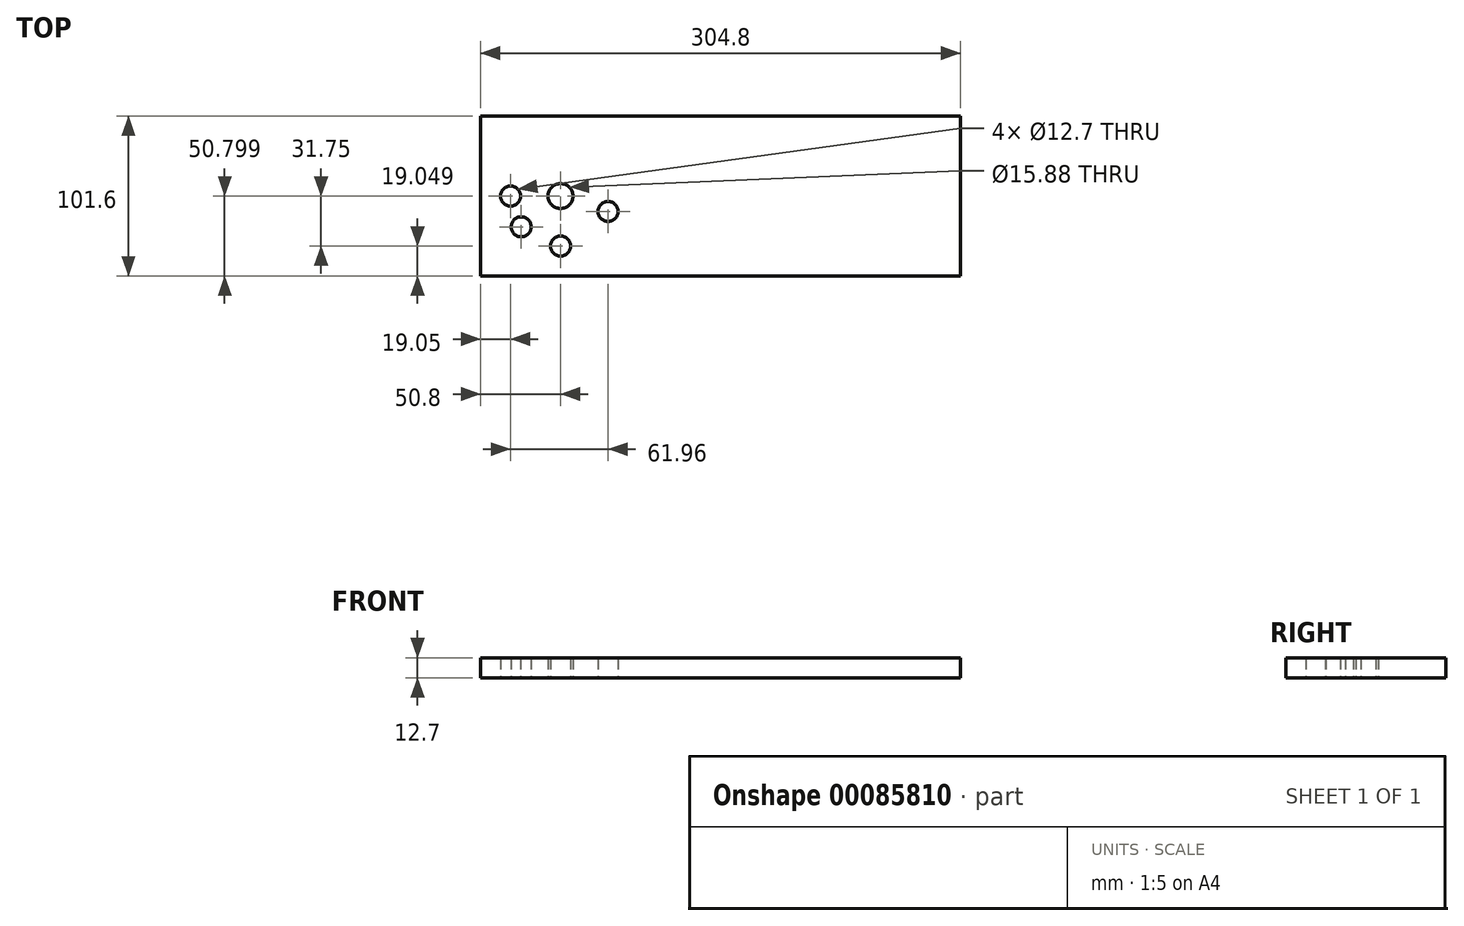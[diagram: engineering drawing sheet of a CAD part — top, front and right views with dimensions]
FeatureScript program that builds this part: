
annotation { "Feature Type Name" : "Feature", "Feature Type Description" : "" }
export const myFeature = defineFeature(function(context is Context, id is Id, definition is map)
    precondition{}
    {
        {
            var Q0;
            Q0=qCreatedBy(makeId("Top.planeOp"),FACE);
            var sketch = newSketch(context, id + "F0", { "sketchPlane" : qUnion([Q0])});
            skPoint(sketch, "E0", {"position": v(-53.4, 28.23) * mm});
            skPoint(sketch, "E1", {"position": v(-53.4, 25.06) * mm});
            skPoint(sketch, "E2", {"position": v(-53.4, 53.63) * mm});
            skPoint(sketch, "E3", {"position": v(-53.4, 12.36) * mm});
            skPoint(sketch, "E4", {"position": v(-53.4, -19.4) * mm});
            skPoint(sketch, "E5", {"position": v(-92.66, 25.06) * mm});
            skPoint(sketch, "E6", {"position": v(-23.18, 2.59) * mm});
            skPoint(sketch, "E7", {"position": v(-85.14, 12.36) * mm});
            skPoint(sketch, "E8", {"position": v(-78.42, -7.18) * mm});
            skPoint(sketch, "E9", {"position": v(-20.86, 37.76) * mm});
            skPoint(sketch, "E10", {"position": v(-12.12, 12.36) * mm});
            skLineSegment(sketch, "E11", {"start": v(-2.6, 63.16) * mm, "end": v(-104.2, 63.16) * mm});
            skLineSegment(sketch, "E12", {"start": v(-104.2, 63.16) * mm, "end": v(-104.2, -38.44) * mm});
            skLineSegment(sketch, "E13", {"start": v(-104.2, -38.44) * mm, "end": v(-2.6, -38.44) * mm});
            skCircle(sketch, "E14", {"center": v(-53.4, 53.63) * mm, "radius": 1.27 * mm});
            skCircle(sketch, "E15", {"center": v(-92.66, 25.06) * mm, "radius": 1.27 * mm});
            skCircle(sketch, "E16", {"center": v(-85.14, 12.36) * mm, "radius": 1.27 * mm});
            skCircle(sketch, "E17", {"center": v(-78.42, -7.18) * mm, "radius": 1.27 * mm});
            skCircle(sketch, "E18", {"center": v(-53.4, -19.4) * mm, "radius": 1.27 * mm});
            skCircle(sketch, "E19", {"center": v(-23.18, 2.59) * mm, "radius": 1.27 * mm});
            skCircle(sketch, "E20", {"center": v(-12.12, 12.36) * mm, "radius": 1.27 * mm});
            skCircle(sketch, "E21", {"center": v(-20.86, 37.76) * mm, "radius": 1.27 * mm});
            skCircle(sketch, "E22", {"center": v(-53.4, 12.36) * mm, "radius": 1.27 * mm});
            skLineSegment(sketch, "E23", {"start": v(200.6, 63.16) * mm, "end": v(200.6, -38.44) * mm});
            skLineSegment(sketch, "E24", {"start": v(-2.6, -38.44) * mm, "end": v(200.6, -38.44) * mm});
            skLineSegment(sketch, "E25", {"start": v(-2.6, 63.16) * mm, "end": v(200.6, 63.16) * mm});
            skSolve(sketch);
        }
        {
            var Q0;
            Q0=makeQuery(id+"F0.imprint","IMPRINT",FACE,{"disambiguationData":[TD([[makeQuery(id+"F0.imprint","IMPRINT",EDGE,{"derivedFrom":sQuery(id+"F0.wireOp",EDGE,"E15")}),1.0]])]});
            var Q1;
            Q1=makeQuery(id+"F0.imprint","IMPRINT",FACE,{"disambiguationData":[TD([[makeQuery(id+"F0.imprint","IMPRINT",EDGE,{"derivedFrom":sQuery(id+"F0.wireOp",EDGE,"E14")}),1.0]])]});
            var Q2;
            Q2=makeQuery(id+"F0.imprint","IMPRINT",FACE,{"disambiguationData":[TD([[makeQuery(id+"F0.imprint","IMPRINT",EDGE,{"derivedFrom":sQuery(id+"F0.wireOp",EDGE,"E21")}),1.0]])]});
            var Q3;
            {var subQ0=sQuery(id+"F0.wireOp",EDGE,"E20");var subQ1=sQuery(id+"F0.wireOp",EDGE,"kDzNyt80-dS94-SnEu-0VYT-oXaxEeU8iF4R");var subQ2=makeQuery(id+"F0.imprint","INTERSECT",VERTEX,{"disambiguationData":[OD(0.0)],"derivedFrom":[subQ1,subQ0]});Q3=makeQuery(id+"F0.imprint","IMPRINT",FACE,{"disambiguationData":[TD([[makeQuery(id+"F0.imprint","IMPRINT",EDGE,{"disambiguationData":[TD([[subQ2,1.0]])],"derivedFrom":subQ1}),-1.0]])]});}
            var Q4;
            {var subQ0=sQuery(id+"F0.wireOp",EDGE,"E20");var subQ1=sQuery(id+"F0.wireOp",EDGE,"kDzNyt80-dS94-SnEu-0VYT-oXaxEeU8iF4R");var subQ2=makeQuery(id+"F0.imprint","INTERSECT",VERTEX,{"disambiguationData":[OD(0.0)],"derivedFrom":[subQ1,subQ0]});Q4=makeQuery(id+"F0.imprint","IMPRINT",FACE,{"disambiguationData":[TD([[makeQuery(id+"F0.imprint","IMPRINT",EDGE,{"disambiguationData":[TD([[subQ2,1.0]])],"derivedFrom":subQ1}),1.0]])]});}
            var Q5;
            Q5=makeQuery(id+"F0.imprint","IMPRINT",FACE,{"disambiguationData":[TD([[makeQuery(id+"F0.imprint","IMPRINT",EDGE,{"derivedFrom":sQuery(id+"F0.wireOp",EDGE,"E11")}),1.0]])]});
            var Q6;
            Q6=makeQuery(id+"F0.imprint","IMPRINT",FACE,{"disambiguationData":[TD([[makeQuery(id+"F0.imprint","IMPRINT",EDGE,{"derivedFrom":sQuery(id+"F0.wireOp",EDGE,"E20")}),1.0]])]});
            extrude(context, id + "F1", {"entities" : qUnion([Q0, Q1, Q2, Q3, Q4, Q5, Q6]), "depth" : 12.7 * mm, "offsetDistance" : 25.4 * mm});
        }
        {
            var Q0;
            Q0=makeQuery(id+"F1.opExtrude","CAP_FACE",FACE,{"disambiguationData":[OSD([sQuery(id+"F0.wireOp",EDGE,"E11"),sQuery(id+"F0.wireOp",EDGE,"E12"),sQuery(id+"F0.wireOp",EDGE,"E13"),sQuery(id+"F0.wireOp",EDGE,"sKdmvjwX-j8QO-bxV5-SpKZ-w8j0p7tcOjNn"),sQuery(id+"F0.wireOp",EDGE,"E14"),sQuery(id+"F0.wireOp",EDGE,"E15"),sQuery(id+"F0.wireOp",EDGE,"E16"),sQuery(id+"F0.wireOp",EDGE,"E17"),sQuery(id+"F0.wireOp",EDGE,"E18"),sQuery(id+"F0.wireOp",EDGE,"E19"),sQuery(id+"F0.wireOp",EDGE,"E20"),sQuery(id+"F0.wireOp",EDGE,"E21"),sQuery(id+"F0.wireOp",EDGE,"E22")])],"isStart":false});
            var sketch = newSketch(context, id + "F2", { "sketchPlane" : qUnion([Q0])});
            skPoint(sketch, "E26", {"position": v(-53.4, 53.63) * mm});
            skPoint(sketch, "E27", {"position": v(-20.86, 37.76) * mm});
            skPoint(sketch, "E28", {"position": v(-12.12, 12.36) * mm});
            skPoint(sketch, "E29", {"position": v(-23.18, 2.59) * mm});
            skPoint(sketch, "E30", {"position": v(-53.4, -19.4) * mm});
            skPoint(sketch, "E31", {"position": v(-78.42, -7.18) * mm});
            skPoint(sketch, "E32", {"position": v(-85.14, 12.36) * mm});
            skPoint(sketch, "E33", {"position": v(-92.66, 25.06) * mm});
            skPoint(sketch, "E34", {"position": v(-53.4, 12.36) * mm});
            skSolve(sketch);
        }
        {
            var Q0;
            Q0=sQuery(id+"F2.wireOp",VERTEX,"E34");
            var Q1;
            Q1=makeQuery(id+"F1.opExtrude","SWEPT_BODY",BODY,{"disambiguationData":[OSD([sQuery(id+"F0.wireOp",EDGE,"E11"),sQuery(id+"F0.wireOp",EDGE,"E12"),sQuery(id+"F0.wireOp",EDGE,"E13"),sQuery(id+"F0.wireOp",EDGE,"sKdmvjwX-j8QO-bxV5-SpKZ-w8j0p7tcOjNn"),sQuery(id+"F0.wireOp",EDGE,"E14"),sQuery(id+"F0.wireOp",EDGE,"E15"),sQuery(id+"F0.wireOp",EDGE,"E16"),sQuery(id+"F0.wireOp",EDGE,"E17"),sQuery(id+"F0.wireOp",EDGE,"E18"),sQuery(id+"F0.wireOp",EDGE,"E19"),sQuery(id+"F0.wireOp",EDGE,"E20"),sQuery(id+"F0.wireOp",EDGE,"E21"),sQuery(id+"F0.wireOp",EDGE,"E22")])]});
            hole(context, id + "F3", {"style" : HoleStyle.SIMPLE, "endStyle" : HoleEndStyle.THROUGH, "holeDiameter" : 15.88 * mm, "majorDiameter" : 6.35 * mm, "tappedDepth" : 12.7 * mm, "tapClearance" : 3, "startFromSketch" : true, "locations" : qUnion([Q0]), "scope" : qUnion([Q1])});
        }
        {
            var Q0;
            Q0=makeQuery(id+"F1.opExtrude","CAP_FACE",FACE,{"disambiguationData":[OSD([sQuery(id+"F0.wireOp",EDGE,"E11"),sQuery(id+"F0.wireOp",EDGE,"E12"),sQuery(id+"F0.wireOp",EDGE,"E13"),sQuery(id+"F0.wireOp",EDGE,"sKdmvjwX-j8QO-bxV5-SpKZ-w8j0p7tcOjNn"),sQuery(id+"F0.wireOp",EDGE,"E14"),sQuery(id+"F0.wireOp",EDGE,"E15"),sQuery(id+"F0.wireOp",EDGE,"E16"),sQuery(id+"F0.wireOp",EDGE,"E17"),sQuery(id+"F0.wireOp",EDGE,"E18"),sQuery(id+"F0.wireOp",EDGE,"E19"),sQuery(id+"F0.wireOp",EDGE,"E20"),sQuery(id+"F0.wireOp",EDGE,"E21"),sQuery(id+"F0.wireOp",EDGE,"E22")])],"isStart":true});
            var sketch = newSketch(context, id + "F4", { "sketchPlane" : qUnion([Q0])});
            skPoint(sketch, "E35", {"position": v(-53.4, -53.63) * mm});
            skSolve(sketch);
        }
        {
            var Q0;
            Q0=makeQuery(id+"F1.opExtrude","CAP_FACE",FACE,{"disambiguationData":[OSD([sQuery(id+"F0.wireOp",EDGE,"E11"),sQuery(id+"F0.wireOp",EDGE,"E12"),sQuery(id+"F0.wireOp",EDGE,"E13"),sQuery(id+"F0.wireOp",EDGE,"sKdmvjwX-j8QO-bxV5-SpKZ-w8j0p7tcOjNn"),sQuery(id+"F0.wireOp",EDGE,"E14"),sQuery(id+"F0.wireOp",EDGE,"E15"),sQuery(id+"F0.wireOp",EDGE,"E16"),sQuery(id+"F0.wireOp",EDGE,"E17"),sQuery(id+"F0.wireOp",EDGE,"E18"),sQuery(id+"F0.wireOp",EDGE,"E19"),sQuery(id+"F0.wireOp",EDGE,"E20"),sQuery(id+"F0.wireOp",EDGE,"E21"),sQuery(id+"F0.wireOp",EDGE,"E22")])],"isStart":false});
            var sketch = newSketch(context, id + "F5", { "sketchPlane" : qUnion([Q0])});
            skPoint(sketch, "E36", {"position": v(-53.4, -19.4) * mm});
            skSolve(sketch);
        }
        {
            var Q0;
            Q0=sQuery(id+"F5.wireOp",VERTEX,"E36");
            var Q1;
            Q1=makeQuery(id+"F1.opExtrude","SWEPT_BODY",BODY,{"disambiguationData":[OSD([sQuery(id+"F0.wireOp",EDGE,"E11"),sQuery(id+"F0.wireOp",EDGE,"E12"),sQuery(id+"F0.wireOp",EDGE,"E13"),sQuery(id+"F0.wireOp",EDGE,"sKdmvjwX-j8QO-bxV5-SpKZ-w8j0p7tcOjNn"),sQuery(id+"F0.wireOp",EDGE,"E14"),sQuery(id+"F0.wireOp",EDGE,"E15"),sQuery(id+"F0.wireOp",EDGE,"E16"),sQuery(id+"F0.wireOp",EDGE,"E17"),sQuery(id+"F0.wireOp",EDGE,"E18"),sQuery(id+"F0.wireOp",EDGE,"E19"),sQuery(id+"F0.wireOp",EDGE,"E20"),sQuery(id+"F0.wireOp",EDGE,"E21"),sQuery(id+"F0.wireOp",EDGE,"E22")])]});
            hole(context, id + "F6", {"style" : HoleStyle.SIMPLE, "endStyle" : HoleEndStyle.THROUGH, "holeDiameter" : 12.7 * mm, "majorDiameter" : 6.35 * mm, "tappedDepth" : 12.7 * mm, "tapClearance" : 3, "startFromSketch" : true, "locations" : qUnion([Q0]), "scope" : qUnion([Q1])});
        }
        {
            var Q0;
            Q0=makeQuery(id+"F1.opExtrude","CAP_FACE",FACE,{"disambiguationData":[OSD([sQuery(id+"F0.wireOp",EDGE,"E11"),sQuery(id+"F0.wireOp",EDGE,"E12"),sQuery(id+"F0.wireOp",EDGE,"E13"),sQuery(id+"F0.wireOp",EDGE,"sKdmvjwX-j8QO-bxV5-SpKZ-w8j0p7tcOjNn"),sQuery(id+"F0.wireOp",EDGE,"E14"),sQuery(id+"F0.wireOp",EDGE,"E15"),sQuery(id+"F0.wireOp",EDGE,"E16"),sQuery(id+"F0.wireOp",EDGE,"E17"),sQuery(id+"F0.wireOp",EDGE,"E18"),sQuery(id+"F0.wireOp",EDGE,"E19"),sQuery(id+"F0.wireOp",EDGE,"E20"),sQuery(id+"F0.wireOp",EDGE,"E21"),sQuery(id+"F0.wireOp",EDGE,"E22")])],"isStart":false});
            var sketch = newSketch(context, id + "F7", { "sketchPlane" : qUnion([Q0])});
            skPoint(sketch, "E37", {"position": v(-78.42, -7.18) * mm});
            skPoint(sketch, "E38", {"position": v(-85.14, 12.36) * mm});
            skPoint(sketch, "E39", {"position": v(-23.18, 2.59) * mm});
            skSolve(sketch);
        }
        {
            var Q0;
            Q0=sQuery(id+"F7.wireOp",VERTEX,"E38");
            var Q1;
            Q1=sQuery(id+"F7.wireOp",VERTEX,"E37");
            var Q2;
            Q2=sQuery(id+"F7.wireOp",VERTEX,"E39");
            var Q3;
            Q3=makeQuery(id+"F1.opExtrude","SWEPT_BODY",BODY,{"disambiguationData":[OSD([sQuery(id+"F0.wireOp",EDGE,"E11"),sQuery(id+"F0.wireOp",EDGE,"E12"),sQuery(id+"F0.wireOp",EDGE,"E13"),sQuery(id+"F0.wireOp",EDGE,"sKdmvjwX-j8QO-bxV5-SpKZ-w8j0p7tcOjNn"),sQuery(id+"F0.wireOp",EDGE,"E14"),sQuery(id+"F0.wireOp",EDGE,"E15"),sQuery(id+"F0.wireOp",EDGE,"E16"),sQuery(id+"F0.wireOp",EDGE,"E17"),sQuery(id+"F0.wireOp",EDGE,"E18"),sQuery(id+"F0.wireOp",EDGE,"E19"),sQuery(id+"F0.wireOp",EDGE,"E20"),sQuery(id+"F0.wireOp",EDGE,"E21"),sQuery(id+"F0.wireOp",EDGE,"E22")])]});
            hole(context, id + "F8", {"style" : HoleStyle.SIMPLE, "endStyle" : HoleEndStyle.THROUGH, "holeDiameter" : 12.7 * mm, "majorDiameter" : 6.35 * mm, "tappedDepth" : 12.7 * mm, "tapClearance" : 3, "startFromSketch" : true, "locations" : qUnion([Q0, Q1, Q2]), "scope" : qUnion([Q3])});
        }
    });
